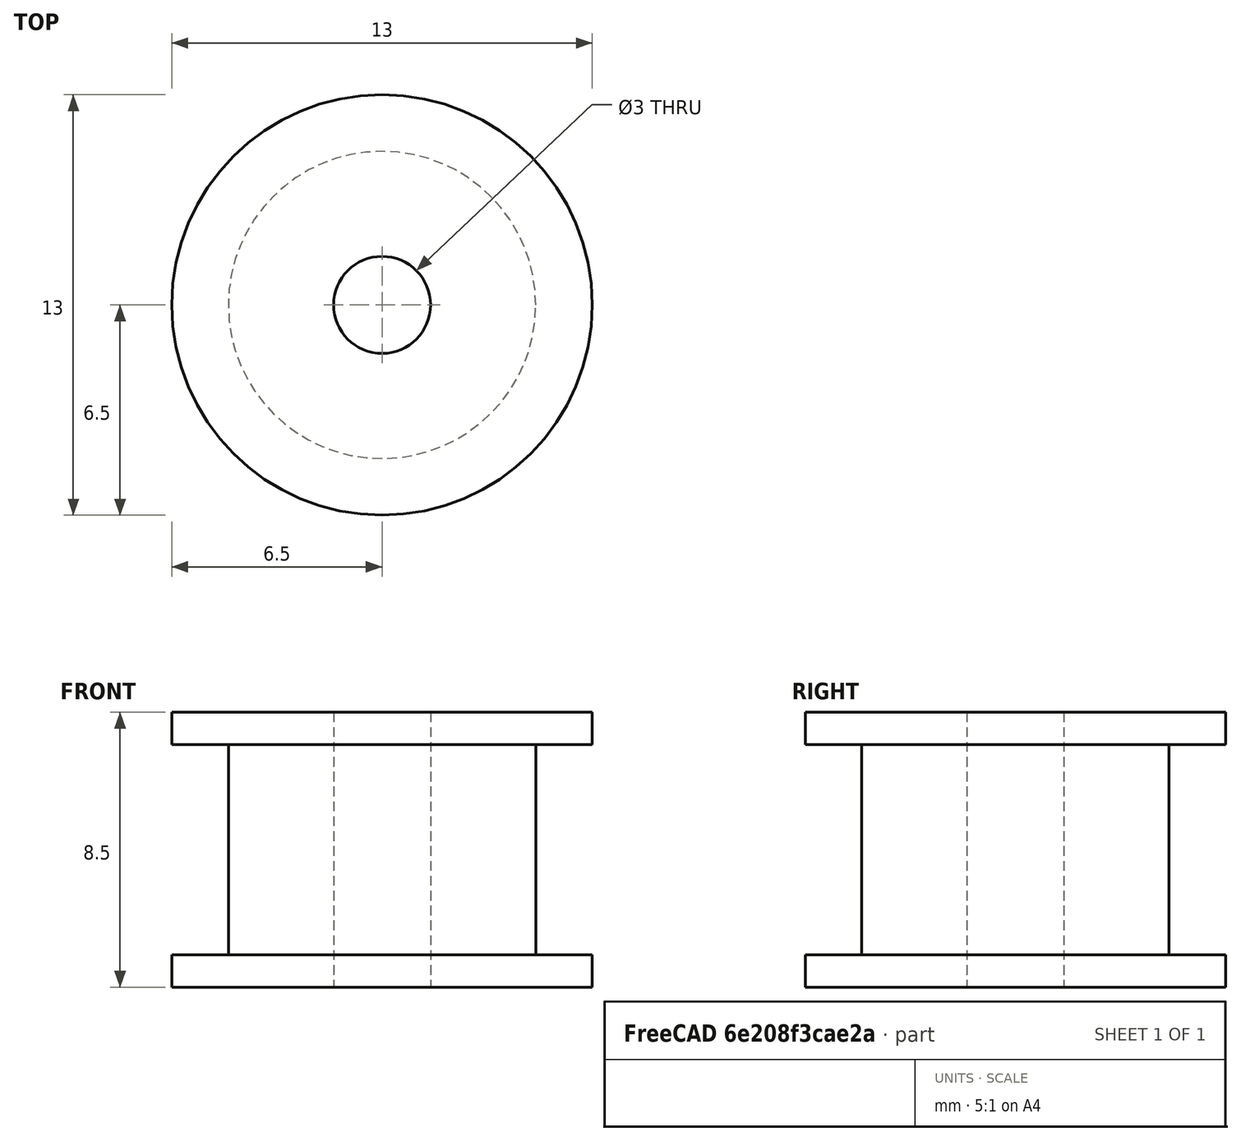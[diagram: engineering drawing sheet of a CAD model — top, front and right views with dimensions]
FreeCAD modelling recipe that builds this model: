
FCSTD DOCUMENT  (FreeCAD 1.0R39109 (Git))
Label: GT2-6mm-NoTeeth-16T-3mmBore
License: All rights reserved
LicenseURL: https://en.wikipedia.org/wiki/All_rights_reserved
objects: Sketcher::SketchObject×1, PartDesign::Revolution×1, PartDesign::Body×1
note: 6 computed .brp shape members not serialized (recipe doc carries the construction recipe); baked Part::Feature solids carry a one-line shape summary decoded from their .brp

FEATURE [Sketcher::SketchObject] Sketch
  ArcFitTolerance = 1e-06
  AttachmentSupport = -> [XZ_Plane]
  FullyConstrained = true
  MakeInternals = false
  MapMode = 5
  Placement = pos=(0,0,0) rot=(1,0,0;1.5708rad)
  sketch-geometry (8):
    g0: LineSegment StartX=-1.5 StartY=0 StartZ=0 EndX=-6.5 EndY=0 EndZ=0
    g1: LineSegment StartX=-6.5 StartY=0 StartZ=0 EndX=-6.5 EndY=1 EndZ=0
    g2: LineSegment StartX=-6.5 StartY=1 StartZ=0 EndX=-4.75 EndY=1 EndZ=0
    g3: LineSegment StartX=-4.75 StartY=1 StartZ=0 EndX=-4.75 EndY=7.5 EndZ=0
    g4: LineSegment StartX=-4.75 StartY=7.5 StartZ=0 EndX=-6.5 EndY=7.5 EndZ=0
    g5: LineSegment StartX=-6.5 StartY=7.5 StartZ=0 EndX=-6.5 EndY=8.5 EndZ=0
    g6: LineSegment StartX=-6.5 StartY=8.5 StartZ=0 EndX=-1.5 EndY=8.5 EndZ=0
    g7: LineSegment StartX=-1.5 StartY=8.5 StartZ=0 EndX=-1.5 EndY=0 EndZ=0
  constraints (24):
    c: PointOnObject(g0,g-1)
    c: Horizontal(g0)
    c: Coincident(g0,g1)
    c: Vertical(g1)
    c: Coincident(g1,g2)
    c: Horizontal(g2)
    c: Coincident(g2,g3)
    c: Vertical(g3)
    c: Coincident(g3,g4)
    c: Horizontal(g4)
    c: Coincident(g4,g5)
    c: Vertical(g5)
    c: Coincident(g5,g6)
    c: Horizontal(g6)
    c: Coincident(g6,g7)
    c: Coincident(g7,g0)
    c: Vertical(g7)
    c: Distance(g-2,g3) = 4.75
    c: Distance(g-2,g7) = 1.5
    c: Distance(g-2,g1) = 6.5
    c: DistanceY(g7,g7) = 8.5
    c: Distance(g3,g3) = 6.5
    c: Equal(g5,g1)
    c: PointOnObject(g4,g1)
FEATURE [PartDesign::Revolution] Revolution
  Angle = 360
  Angle2 = 60
  Axis = (0,2e-16,1)
  Base = (0,0,0)
  Placement = pos=(0,0,0) rot=(1,0,0;1.5708rad)
  Profile = -> Sketch
  ReferenceAxis = -> Sketch [V_Axis]
  Refine = true
  Suppressed = false
  Type = 0
FEATURE [PartDesign::Body] Body
  AllowCompound = false
  Group = -> [Sketch,Revolution]
  Origin = -> Origin
  Tip = -> Revolution
